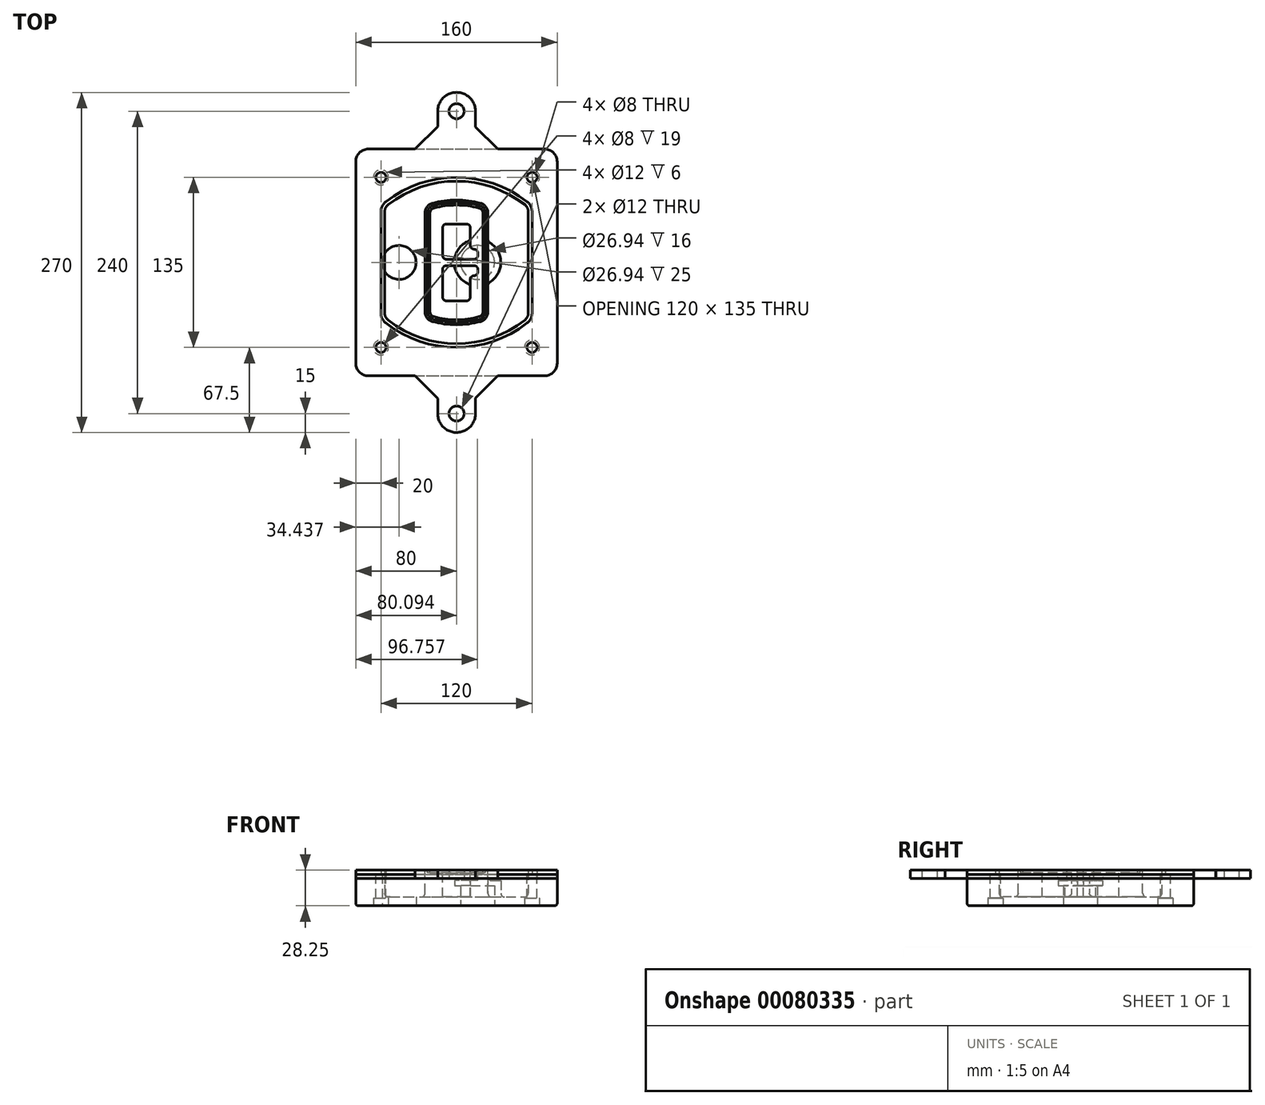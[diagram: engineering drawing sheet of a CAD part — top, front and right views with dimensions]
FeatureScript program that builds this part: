
annotation { "Feature Type Name" : "Feature", "Feature Type Description" : "" }
export const myFeature = defineFeature(function(context is Context, id is Id, definition is map)
    precondition{}
    {
        {
            var Q0;
            Q0=qCreatedBy(makeId("Top.planeOp"),FACE);
            var sketch = newSketch(context, id + "F0", { "sketchPlane" : qUnion([Q0])});
            skPoint(sketch, "E0.rect.middle", {"position": v(0, 0) * mm});
            skLineSegment(sketch, "E1.bottom", {"start": v(-70, -90) * mm, "end": v(70, -90) * mm});
            skLineSegment(sketch, "E1.top", {"start": v(-70, 90) * mm, "end": v(70, 90) * mm});
            skLineSegment(sketch, "E1.left", {"start": v(-80, -80) * mm, "end": v(-80, 80) * mm});
            skLineSegment(sketch, "E1.right", {"start": v(80, -80) * mm, "end": v(80, 80) * mm});
            skLineSegment(sketch, "E2", {"start": v(-80, 90) * mm, "end": v(80, -90) * mm, "construction": true});
            skLineSegment(sketch, "E3", {"start": v(80, 90) * mm, "end": v(-80, -90) * mm, "construction": true});
            skCircle(sketch, "E4", {"center": v(-60, 67.5) * mm, "radius": 4 * mm});
            skCircle(sketch, "E5", {"center": v(60, 67.5) * mm, "radius": 4 * mm});
            skCircle(sketch, "E6", {"center": v(60, -67.5) * mm, "radius": 4 * mm});
            skCircle(sketch, "E7", {"center": v(-60, -67.5) * mm, "radius": 4 * mm});
            skLineSegment(sketch, "E8", {"start": v(-60, 67.5) * mm, "end": v(60, 67.5) * mm, "construction": true});
            skLineSegment(sketch, "E9", {"start": v(60, 67.5) * mm, "end": v(60, -67.5) * mm, "construction": true});
            skLineSegment(sketch, "E10", {"start": v(60, -67.5) * mm, "end": v(-60, -67.5) * mm, "construction": true});
            skLineSegment(sketch, "E11", {"start": v(-60, -67.5) * mm, "end": v(-60, 67.5) * mm, "construction": true});
            skLineSegment(sketch, "E12", {"start": v(-60, 40.3) * mm, "end": v(-60, -40.3) * mm});
            skLineSegment(sketch, "E13", {"start": v(60, 40.3) * mm, "end": v(60, -40.3) * mm});
            skArc(sketch, "E14", {"start": v(56.15, 48.18) * mm, "mid": v(0, 67.5) * mm, "end": v(-56.15, 48.18) * mm});
            skArc(sketch, "E15", {"start": v(-56.15, -48.18) * mm, "mid": v(0, -67.5) * mm, "end": v(56.15, -48.18) * mm});
            skLineSegment(sketch, "E16", {"start": v(-60, 0) * mm, "end": v(60, 0) * mm, "construction": true});
            skPoint(sketch, "E17.visualSharp", {"position": v(-60, -45) * mm});
            skArc(sketch, "E17.filletArc", {"start": v(-60, -40.3) * mm, "mid": v(-58.99, -44.68) * mm, "end": v(-56.15, -48.18) * mm});
            skPoint(sketch, "E18.visualSharp", {"position": v(-60, 45) * mm});
            skArc(sketch, "E18.filletArc", {"start": v(-56.15, 48.18) * mm, "mid": v(-58.99, 44.68) * mm, "end": v(-60, 40.3) * mm});
            skPoint(sketch, "E19.visualSharp", {"position": v(60, 45) * mm});
            skArc(sketch, "E19.filletArc", {"start": v(60, 40.3) * mm, "mid": v(58.99, 44.68) * mm, "end": v(56.15, 48.18) * mm});
            skPoint(sketch, "E20.visualSharp", {"position": v(60, -45) * mm});
            skArc(sketch, "E20.filletArc", {"start": v(56.15, -48.18) * mm, "mid": v(58.99, -44.68) * mm, "end": v(60, -40.3) * mm});
            skPoint(sketch, "E21.visualSharp", {"position": v(-80, 90) * mm});
            skArc(sketch, "E21.filletArc", {"start": v(-70, 90) * mm, "mid": v(-77.07, 87.07) * mm, "end": v(-80, 80) * mm});
            skPoint(sketch, "E22.visualSharp", {"position": v(80, 90) * mm});
            skArc(sketch, "E22.filletArc", {"start": v(80, 80) * mm, "mid": v(77.07, 87.07) * mm, "end": v(70, 90) * mm});
            skPoint(sketch, "E23.visualSharp", {"position": v(80, -90) * mm});
            skArc(sketch, "E23.filletArc", {"start": v(70, -90) * mm, "mid": v(77.07, -87.07) * mm, "end": v(80, -80) * mm});
            skPoint(sketch, "E24.visualSharp", {"position": v(-80, -90) * mm});
            skArc(sketch, "E24.filletArc", {"start": v(-80, -80) * mm, "mid": v(-77.07, -87.07) * mm, "end": v(-70, -90) * mm});
            skArc(sketch, "E25.0", {"start": v(57, 40.3) * mm, "mid": v(56.3, 43.36) * mm, "end": v(54.3, 45.81) * mm});
            skLineSegment(sketch, "E25.1", {"start": v(57, 40.3) * mm, "end": v(57, -40.3) * mm});
            skArc(sketch, "E25.2", {"start": v(54.3, -45.81) * mm, "mid": v(56.3, -43.36) * mm, "end": v(57, -40.3) * mm});
            skArc(sketch, "E25.3", {"start": v(-54.3, -45.81) * mm, "mid": v(0, -64.5) * mm, "end": v(54.3, -45.81) * mm});
            skArc(sketch, "E25.4", {"start": v(-57, -40.3) * mm, "mid": v(-56.3, -43.36) * mm, "end": v(-54.3, -45.81) * mm});
            skArc(sketch, "E25.5", {"start": v(54.3, 45.81) * mm, "mid": v(0, 64.5) * mm, "end": v(-54.3, 45.81) * mm});
            skLineSegment(sketch, "E25.6", {"start": v(-57, 40.3) * mm, "end": v(-57, -40.3) * mm});
            skArc(sketch, "E25.7", {"start": v(-54.3, 45.81) * mm, "mid": v(-56.3, 43.36) * mm, "end": v(-57, 40.3) * mm});
            skArc(sketch, "E26.0", {"start": v(-58.62, 51.33) * mm, "mid": v(-62.58, 46.43) * mm, "end": v(-64, 40.3) * mm});
            skArc(sketch, "E26.1", {"start": v(58.62, 51.33) * mm, "mid": v(0, 71.5) * mm, "end": v(-58.62, 51.33) * mm});
            skArc(sketch, "E26.2", {"start": v(64, 40.3) * mm, "mid": v(62.58, 46.43) * mm, "end": v(58.62, 51.33) * mm});
            skLineSegment(sketch, "E26.3", {"start": v(64, 40.3) * mm, "end": v(64, -40.3) * mm});
            skArc(sketch, "E26.4", {"start": v(58.62, -51.33) * mm, "mid": v(62.58, -46.43) * mm, "end": v(64, -40.3) * mm});
            skLineSegment(sketch, "E26.5", {"start": v(-64, 40.3) * mm, "end": v(-64, -40.3) * mm});
            skArc(sketch, "E26.6", {"start": v(-58.62, -51.33) * mm, "mid": v(0, -71.5) * mm, "end": v(58.62, -51.33) * mm});
            skArc(sketch, "E26.7", {"start": v(-64, -40.3) * mm, "mid": v(-62.58, -46.43) * mm, "end": v(-58.62, -51.33) * mm});
            skSolve(sketch);
        }
        {
            var Q0;
            Q0=makeQuery(id+"F0.imprint","IMPRINT",FACE,{"disambiguationData":[TD([[makeQuery(id+"F0.imprint","IMPRINT",EDGE,{"derivedFrom":sQuery(id+"F0.wireOp",EDGE,"E1.bottom")}),1.0]])]});
            var Q1;
            Q1=makeQuery(id+"F0.imprint","IMPRINT",FACE,{"disambiguationData":[TD([[makeQuery(id+"F0.imprint","IMPRINT",EDGE,{"derivedFrom":sQuery(id+"F0.wireOp",EDGE,"E12")}),1.0]])]});
            var Q2;
            Q2=makeQuery(id+"F0.imprint","IMPRINT",FACE,{"disambiguationData":[TD([[makeQuery(id+"F0.imprint","IMPRINT",EDGE,{"derivedFrom":sQuery(id+"F0.wireOp",EDGE,"E25.0")}),1.0]])]});
            var Q3;
            Q3=makeQuery(id+"F0.imprint","IMPRINT",FACE,{"disambiguationData":[TD([[makeQuery(id+"F0.imprint","IMPRINT",EDGE,{"derivedFrom":sQuery(id+"F0.wireOp",EDGE,"E12")}),-1.0]])]});
            extrude(context, id + "F1", {"entities" : qUnion([Q0, Q1, Q2, Q3]), "oppositeDirection" : true, "depth" : 25 * mm});
        }
        {
            var Q0;
            Q0=makeQuery(id+"F0.imprint","IMPRINT",FACE,{"disambiguationData":[TD([[makeQuery(id+"F0.imprint","IMPRINT",EDGE,{"derivedFrom":sQuery(id+"F0.wireOp",EDGE,"E12")}),1.0]])]});
            extrude(context, id + "F2", {"entities" : qUnion([Q0]), "operationType" : NewBodyOperationType.ADD, "depth" : 3 * mm});
        }
        {
            var Q0;
            Q0=makeQuery(id+"F0.imprint","IMPRINT",FACE,{"disambiguationData":[TD([[makeQuery(id+"F0.imprint","IMPRINT",EDGE,{"derivedFrom":sQuery(id+"F0.wireOp",EDGE,"E25.0")}),1.0]])]});
            extrude(context, id + "F3", {"entities" : qUnion([Q0]), "operationType" : NewBodyOperationType.REMOVE, "oppositeDirection" : true, "depth" : 18 * mm});
        }
        {
            var Q0;
            Q0=makeQuery(id+"F2.opExtrude","CAP_FACE",FACE,{"disambiguationData":[OSD([sQuery(id+"F0.wireOp",EDGE,"E12"),sQuery(id+"F0.wireOp",EDGE,"E13"),sQuery(id+"F0.wireOp",EDGE,"E14"),sQuery(id+"F0.wireOp",EDGE,"E15"),sQuery(id+"F0.wireOp",EDGE,"E17.filletArc"),sQuery(id+"F0.wireOp",EDGE,"E18.filletArc"),sQuery(id+"F0.wireOp",EDGE,"E19.filletArc"),sQuery(id+"F0.wireOp",EDGE,"E20.filletArc"),sQuery(id+"F0.wireOp",EDGE,"E25.0"),sQuery(id+"F0.wireOp",EDGE,"E25.1"),sQuery(id+"F0.wireOp",EDGE,"E25.2"),sQuery(id+"F0.wireOp",EDGE,"E25.3"),sQuery(id+"F0.wireOp",EDGE,"E25.4"),sQuery(id+"F0.wireOp",EDGE,"E25.5"),sQuery(id+"F0.wireOp",EDGE,"E25.6"),sQuery(id+"F0.wireOp",EDGE,"E25.7")])],"isStart":false});
            var sketch = newSketch(context, id + "F4", { "sketchPlane" : qUnion([Q0])});
            skArc(sketch, "E27.0", {"start": v(-19.08, -46.97) * mm, "mid": v(0, -49.5) * mm, "end": v(19.08, -46.97) * mm});
            skArc(sketch, "E28.0", {"start": v(19.08, 46.97) * mm, "mid": v(0, 49.5) * mm, "end": v(-19.08, 46.97) * mm});
            skLineSegment(sketch, "E29", {"start": v(-25, 39.25) * mm, "end": v(-25, -39.25) * mm});
            skLineSegment(sketch, "E30", {"start": v(25, 39.25) * mm, "end": v(25, -39.25) * mm});
            skLineSegment(sketch, "E31", {"start": v(-25, 45.1) * mm, "end": v(25, 45.1) * mm, "construction": true});
            skLineSegment(sketch, "E32", {"start": v(-25, -45.1) * mm, "end": v(25, -45.1) * mm, "construction": true});
            skPoint(sketch, "E33.visualSharp", {"position": v(-25, 45.1) * mm});
            skArc(sketch, "E33.filletArc", {"start": v(-19.08, 46.97) * mm, "mid": v(-23.35, 44.11) * mm, "end": v(-25, 39.25) * mm});
            skPoint(sketch, "E34.visualSharp", {"position": v(25, 45.1) * mm});
            skArc(sketch, "E34.filletArc", {"start": v(25, 39.25) * mm, "mid": v(23.35, 44.11) * mm, "end": v(19.08, 46.97) * mm});
            skPoint(sketch, "E35.visualSharp", {"position": v(25, -45.1) * mm});
            skArc(sketch, "E35.filletArc", {"start": v(19.08, -46.97) * mm, "mid": v(23.35, -44.11) * mm, "end": v(25, -39.25) * mm});
            skPoint(sketch, "E36.visualSharp", {"position": v(-25, -45.1) * mm});
            skArc(sketch, "E36.filletArc", {"start": v(-25, -39.25) * mm, "mid": v(-23.35, -44.11) * mm, "end": v(-19.08, -46.97) * mm});
            skArc(sketch, "E37.0", {"start": v(54.3, 45.81) * mm, "mid": v(0, 64.5) * mm, "end": v(-54.3, 45.81) * mm});
            skArc(sketch, "E37.1", {"start": v(-54.3, 45.81) * mm, "mid": v(-56.3, 43.36) * mm, "end": v(-57, 40.3) * mm});
            skLineSegment(sketch, "E37.2", {"start": v(-57, 40.3) * mm, "end": v(-57, -40.3) * mm});
            skArc(sketch, "E37.3", {"start": v(-57, -40.3) * mm, "mid": v(-56.3, -43.36) * mm, "end": v(-54.3, -45.81) * mm});
            skArc(sketch, "E37.4", {"start": v(-54.3, -45.81) * mm, "mid": v(0, -64.5) * mm, "end": v(54.3, -45.81) * mm});
            skArc(sketch, "E37.5", {"start": v(54.3, -45.81) * mm, "mid": v(56.3, -43.36) * mm, "end": v(57, -40.3) * mm});
            skLineSegment(sketch, "E37.6", {"start": v(57, 40.3) * mm, "end": v(57, -40.3) * mm});
            skArc(sketch, "E37.7", {"start": v(57, 40.3) * mm, "mid": v(56.3, 43.36) * mm, "end": v(54.3, 45.81) * mm});
            skLineSegment(sketch, "E38.0", {"start": v(23, 39.25) * mm, "end": v(23, -39.25) * mm});
            skArc(sketch, "E38.1", {"start": v(18.56, -45.04) * mm, "mid": v(21.76, -42.9) * mm, "end": v(23, -39.25) * mm});
            skArc(sketch, "E38.2", {"start": v(-18.56, -45.04) * mm, "mid": v(0, -47.5) * mm, "end": v(18.56, -45.04) * mm});
            skArc(sketch, "E38.3", {"start": v(-23, -39.25) * mm, "mid": v(-21.76, -42.9) * mm, "end": v(-18.56, -45.04) * mm});
            skLineSegment(sketch, "E38.4", {"start": v(-23, 39.25) * mm, "end": v(-23, -39.25) * mm});
            skArc(sketch, "E38.5", {"start": v(23, 39.25) * mm, "mid": v(21.76, 42.9) * mm, "end": v(18.56, 45.04) * mm});
            skArc(sketch, "E38.6", {"start": v(-18.56, 45.04) * mm, "mid": v(-21.76, 42.9) * mm, "end": v(-23, 39.25) * mm});
            skArc(sketch, "E38.7", {"start": v(18.56, 45.04) * mm, "mid": v(0, 47.5) * mm, "end": v(-18.56, 45.04) * mm});
            skArc(sketch, "E39.0", {"start": v(21, 39.25) * mm, "mid": v(20.18, 41.68) * mm, "end": v(18.04, 43.1) * mm});
            skLineSegment(sketch, "E39.1", {"start": v(21, 39.25) * mm, "end": v(21, -39.25) * mm});
            skArc(sketch, "E39.2", {"start": v(18.04, -43.1) * mm, "mid": v(20.18, -41.68) * mm, "end": v(21, -39.25) * mm});
            skArc(sketch, "E39.3", {"start": v(-18.04, -43.1) * mm, "mid": v(0, -45.5) * mm, "end": v(18.04, -43.1) * mm});
            skArc(sketch, "E39.4", {"start": v(-21, -39.25) * mm, "mid": v(-20.18, -41.68) * mm, "end": v(-18.04, -43.1) * mm});
            skArc(sketch, "E39.5", {"start": v(18.04, 43.1) * mm, "mid": v(0, 45.5) * mm, "end": v(-18.04, 43.1) * mm});
            skLineSegment(sketch, "E39.6", {"start": v(-21, 39.25) * mm, "end": v(-21, -39.25) * mm});
            skArc(sketch, "E39.7", {"start": v(-18.04, 43.1) * mm, "mid": v(-20.18, 41.68) * mm, "end": v(-21, 39.25) * mm});
            skLineSegment(sketch, "E40", {"start": v(-25, 0) * mm, "end": v(25, 0) * mm, "construction": true});
            skLineSegment(sketch, "E41", {"start": v(-11, 5.5) * mm, "end": v(-11, 27.5) * mm});
            skLineSegment(sketch, "E42", {"start": v(-8, 30.5) * mm, "end": v(8, 30.5) * mm});
            skLineSegment(sketch, "E43", {"start": v(11, 27.5) * mm, "end": v(11, 13.5) * mm});
            skLineSegment(sketch, "E44", {"start": v(14, 10.5) * mm, "end": v(14, 10.5) * mm});
            skLineSegment(sketch, "E45", {"start": v(17, 7.5) * mm, "end": v(17, 5.5) * mm});
            skLineSegment(sketch, "E46", {"start": v(14, 2.5) * mm, "end": v(-8, 2.5) * mm});
            skPoint(sketch, "E47.visualSharp", {"position": v(-11, 30.5) * mm});
            skArc(sketch, "E47.filletArc", {"start": v(-8, 30.5) * mm, "mid": v(-10.12, 29.62) * mm, "end": v(-11, 27.5) * mm});
            skPoint(sketch, "E48.visualSharp", {"position": v(11, 30.5) * mm});
            skArc(sketch, "E48.filletArc", {"start": v(11, 27.5) * mm, "mid": v(10.12, 29.62) * mm, "end": v(8, 30.5) * mm});
            skPoint(sketch, "E49.visualSharp", {"position": v(11, 10.5) * mm});
            skArc(sketch, "E49.filletArc", {"start": v(11, 13.5) * mm, "mid": v(11.88, 11.38) * mm, "end": v(14, 10.5) * mm});
            skPoint(sketch, "E50.visualSharp", {"position": v(17, 10.5) * mm});
            skArc(sketch, "E50.filletArc", {"start": v(17, 7.5) * mm, "mid": v(16.12, 9.62) * mm, "end": v(14, 10.5) * mm});
            skPoint(sketch, "E51.visualSharp", {"position": v(17, 2.5) * mm});
            skArc(sketch, "E51.filletArc", {"start": v(14, 2.5) * mm, "mid": v(16.12, 3.38) * mm, "end": v(17, 5.5) * mm});
            skPoint(sketch, "E52.visualSharp", {"position": v(-11, 2.5) * mm});
            skArc(sketch, "E52.filletArc", {"start": v(-11, 5.5) * mm, "mid": v(-10.12, 3.38) * mm, "end": v(-8, 2.5) * mm});
            skLineSegment(sketch, "E53.0.MirrorCS", {"start": v(14, -2.5) * mm, "end": v(-8, -2.5) * mm});
            skArc(sketch, "E54.0.MirrorCS", {"start": v(-11, -5.5) * mm, "mid": v(-10.12, -3.38) * mm, "end": v(-8, -2.5) * mm});
            skLineSegment(sketch, "E55.0.MirrorCS", {"start": v(-11, -5.5) * mm, "end": v(-11, -27.5) * mm});
            skArc(sketch, "E56.0.MirrorCS", {"start": v(-8, -30.5) * mm, "mid": v(-10.12, -29.62) * mm, "end": v(-11, -27.5) * mm});
            skLineSegment(sketch, "E57.0.MirrorCS", {"start": v(-8, -30.5) * mm, "end": v(8, -30.5) * mm});
            skArc(sketch, "E58.0.MirrorCS", {"start": v(11, -27.5) * mm, "mid": v(10.12, -29.62) * mm, "end": v(8, -30.5) * mm});
            skLineSegment(sketch, "E59.0.MirrorCS", {"start": v(11, -27.5) * mm, "end": v(11, -13.5) * mm});
            skArc(sketch, "E60.0.MirrorCS", {"start": v(11, -13.5) * mm, "mid": v(11.88, -11.38) * mm, "end": v(14, -10.5) * mm});
            skArc(sketch, "E61.0.MirrorCS", {"start": v(17, -7.5) * mm, "mid": v(16.12, -9.62) * mm, "end": v(14, -10.5) * mm});
            skLineSegment(sketch, "E62.0.MirrorCS", {"start": v(17, -7.5) * mm, "end": v(17, -5.5) * mm});
            skArc(sketch, "E63.0.MirrorCS", {"start": v(14, -2.5) * mm, "mid": v(16.12, -3.38) * mm, "end": v(17, -5.5) * mm});
            skSolve(sketch);
        }
        {
            var Q0;
            Q0=makeQuery(id+"F4.imprint","IMPRINT",FACE,{"disambiguationData":[TD([[makeQuery(id+"F4.imprint","IMPRINT",EDGE,{"derivedFrom":sQuery(id+"F4.wireOp",EDGE,"E27.0")}),1.0]])]});
            var Q1;
            Q1=makeQuery(id+"F4.imprint","IMPRINT",FACE,{"disambiguationData":[TD([[makeQuery(id+"F4.imprint","IMPRINT",EDGE,{"derivedFrom":sQuery(id+"F4.wireOp",EDGE,"E38.0")}),-1.0]])]});
            var Q2;
            Q2=makeQuery(id+"F4.imprint","IMPRINT",FACE,{"disambiguationData":[TD([[makeQuery(id+"F4.imprint","IMPRINT",EDGE,{"derivedFrom":sQuery(id+"F4.wireOp",EDGE,"E39.0")}),1.0]])]});
            extrude(context, id + "F5", {"entities" : qUnion([Q0, Q1, Q2]), "operationType" : NewBodyOperationType.ADD, "endBound" : BoundingType.UP_TO_NEXT, "oppositeDirection" : true, "depth" : 25 * mm});
        }
        {
            var Q0;
            Q0=makeQuery(id+"F4.imprint","IMPRINT",FACE,{"disambiguationData":[TD([[makeQuery(id+"F4.imprint","IMPRINT",EDGE,{"derivedFrom":sQuery(id+"F4.wireOp",EDGE,"E38.0")}),-1.0]])]});
            extrude(context, id + "F6", {"entities" : qUnion([Q0]), "operationType" : NewBodyOperationType.REMOVE, "oppositeDirection" : true, "depth" : 2 * mm});
        }
        {
            var Q0;
            Q0=makeQuery(id+"F1.opExtrude","CAP_FACE",FACE,{"disambiguationData":[OSD([sQuery(id+"F0.wireOp",EDGE,"E1.bottom"),sQuery(id+"F0.wireOp",EDGE,"E1.top"),sQuery(id+"F0.wireOp",EDGE,"E1.left"),sQuery(id+"F0.wireOp",EDGE,"E1.right"),sQuery(id+"F0.wireOp",EDGE,"E4"),sQuery(id+"F0.wireOp",EDGE,"E5"),sQuery(id+"F0.wireOp",EDGE,"E6"),sQuery(id+"F0.wireOp",EDGE,"E7"),sQuery(id+"F0.wireOp",EDGE,"E21.filletArc"),sQuery(id+"F0.wireOp",EDGE,"E22.filletArc"),sQuery(id+"F0.wireOp",EDGE,"E23.filletArc"),sQuery(id+"F0.wireOp",EDGE,"E24.filletArc")])],"isStart":false});
            var sketch = newSketch(context, id + "F7", { "sketchPlane" : qUnion([Q0])});
            skCircle(sketch, "E64", {"center": v(16.76, 0) * mm, "radius": 13.47 * mm});
            skCircle(sketch, "E65", {"center": v(-45.56, 0) * mm, "radius": 13.47 * mm});
            skLineSegment(sketch, "E66", {"start": v(80, 0) * mm, "end": v(-80, 0) * mm});
            skCircle(sketch, "E67", {"center": v(16.76, 0) * mm, "radius": 18.47 * mm});
            skCircle(sketch, "E68", {"center": v(60, -67.5) * mm, "radius": 6 * mm});
            skCircle(sketch, "E69", {"center": v(-60, -67.5) * mm, "radius": 6 * mm});
            skCircle(sketch, "E70", {"center": v(-60, 67.5) * mm, "radius": 6 * mm});
            skCircle(sketch, "E71", {"center": v(60, 67.5) * mm, "radius": 6 * mm});
            skSolve(sketch);
        }
        {
            var Q0;
            {var subQ1=sQuery(id+"F7.wireOp",EDGE,"E66");var subQ4=sQuery(id+"F7.wireOp",EDGE,"E64");var subQ6=makeQuery(id+"F7.imprint","INTERSECT",VERTEX,{"disambiguationData":[OD(0.0)],"derivedFrom":[subQ4,subQ1]});Q0=makeQuery(id+"F7.imprint","IMPRINT",FACE,{"disambiguationData":[TD([[makeQuery(id+"F7.imprint","IMPRINT",EDGE,{"disambiguationData":[TD([[subQ6,-1.0]])],"derivedFrom":subQ4}),-1.0]])]});}
            var Q1;
            {var subQ0=sQuery(id+"F7.wireOp",EDGE,"E66");var subQ1=sQuery(id+"F7.wireOp",EDGE,"E64");var subQ3=makeQuery(id+"F7.imprint","INTERSECT",VERTEX,{"disambiguationData":[OD(0.0)],"derivedFrom":[subQ1,subQ0]});Q1=makeQuery(id+"F7.imprint","IMPRINT",FACE,{"disambiguationData":[TD([[makeQuery(id+"F7.imprint","IMPRINT",EDGE,{"disambiguationData":[TD([[subQ3,-1.0]])],"derivedFrom":subQ1}),1.0]])]});}
            var Q2;
            {var subQ0=sQuery(id+"F7.wireOp",EDGE,"E66");var subQ1=sQuery(id+"F7.wireOp",EDGE,"E64");var subQ3=makeQuery(id+"F7.imprint","INTERSECT",VERTEX,{"disambiguationData":[OD(0.0)],"derivedFrom":[subQ1,subQ0]});Q2=makeQuery(id+"F7.imprint","IMPRINT",FACE,{"disambiguationData":[TD([[makeQuery(id+"F7.imprint","IMPRINT",EDGE,{"disambiguationData":[TD([[subQ3,1.0]])],"derivedFrom":subQ1}),1.0]])]});}
            var Q3;
            {var subQ1=sQuery(id+"F7.wireOp",EDGE,"E66");var subQ4=sQuery(id+"F7.wireOp",EDGE,"E64");var subQ6=makeQuery(id+"F7.imprint","INTERSECT",VERTEX,{"disambiguationData":[OD(0.0)],"derivedFrom":[subQ4,subQ1]});Q3=makeQuery(id+"F7.imprint","IMPRINT",FACE,{"disambiguationData":[TD([[makeQuery(id+"F7.imprint","IMPRINT",EDGE,{"disambiguationData":[TD([[subQ6,1.0]])],"derivedFrom":subQ4}),-1.0]])]});}
            extrude(context, id + "F8", {"entities" : qUnion([Q0, Q1, Q2, Q3]), "operationType" : NewBodyOperationType.ADD, "oppositeDirection" : true, "depth" : 20 * mm});
        }
        {
            var Q0;
            {var subQ0=sQuery(id+"F7.wireOp",EDGE,"E66");var subQ1=sQuery(id+"F7.wireOp",EDGE,"E64");var subQ3=makeQuery(id+"F7.imprint","INTERSECT",VERTEX,{"disambiguationData":[OD(0.0)],"derivedFrom":[subQ1,subQ0]});Q0=makeQuery(id+"F7.imprint","IMPRINT",FACE,{"disambiguationData":[TD([[makeQuery(id+"F7.imprint","IMPRINT",EDGE,{"disambiguationData":[TD([[subQ3,-1.0]])],"derivedFrom":subQ1}),1.0]])]});}
            var Q1;
            {var subQ0=sQuery(id+"F7.wireOp",EDGE,"E66");var subQ1=sQuery(id+"F7.wireOp",EDGE,"E64");var subQ3=makeQuery(id+"F7.imprint","INTERSECT",VERTEX,{"disambiguationData":[OD(0.0)],"derivedFrom":[subQ1,subQ0]});Q1=makeQuery(id+"F7.imprint","IMPRINT",FACE,{"disambiguationData":[TD([[makeQuery(id+"F7.imprint","IMPRINT",EDGE,{"disambiguationData":[TD([[subQ3,1.0]])],"derivedFrom":subQ1}),1.0]])]});}
            extrude(context, id + "F9", {"entities" : qUnion([Q0, Q1]), "operationType" : NewBodyOperationType.REMOVE, "oppositeDirection" : true, "depth" : 16 * mm});
        }
        {
            var Q0;
            {var subQ0=sQuery(id+"F7.wireOp",EDGE,"E66");var subQ1=sQuery(id+"F7.wireOp",EDGE,"E65");var subQ3=makeQuery(id+"F7.imprint","INTERSECT",VERTEX,{"disambiguationData":[OD(0.0)],"derivedFrom":[subQ1,subQ0]});Q0=makeQuery(id+"F7.imprint","IMPRINT",FACE,{"disambiguationData":[TD([[makeQuery(id+"F7.imprint","IMPRINT",EDGE,{"disambiguationData":[TD([[subQ3,-1.0]])],"derivedFrom":subQ1}),1.0]])]});}
            var Q1;
            {var subQ0=sQuery(id+"F7.wireOp",EDGE,"E66");var subQ1=sQuery(id+"F7.wireOp",EDGE,"E65");var subQ3=makeQuery(id+"F7.imprint","INTERSECT",VERTEX,{"disambiguationData":[OD(0.0)],"derivedFrom":[subQ1,subQ0]});Q1=makeQuery(id+"F7.imprint","IMPRINT",FACE,{"disambiguationData":[TD([[makeQuery(id+"F7.imprint","IMPRINT",EDGE,{"disambiguationData":[TD([[subQ3,1.0]])],"derivedFrom":subQ1}),1.0]])]});}
            extrude(context, id + "F10", {"entities" : qUnion([Q0, Q1]), "operationType" : NewBodyOperationType.REMOVE, "oppositeDirection" : true, "depth" : 25 * mm});
        }
        {
            var Q0;
            Q0=makeQuery(id+"F7.imprint","IMPRINT",FACE,{"disambiguationData":[TD([[makeQuery(id+"F7.imprint","IMPRINT",EDGE,{"derivedFrom":sQuery(id+"F7.wireOp",EDGE,"E68")}),1.0]])]});
            var Q1;
            Q1=makeQuery(id+"F7.imprint","IMPRINT",FACE,{"disambiguationData":[TD([[makeQuery(id+"F7.imprint","IMPRINT",EDGE,{"derivedFrom":makeQuery(id+"F1.opExtrude","CAP_EDGE",EDGE,{"disambiguationData":[OSD([sQuery(id+"F0.wireOp",EDGE,"E5")])],"isStart":false})}),-1.0]])]});
            var Q2;
            Q2=makeQuery(id+"F7.imprint","IMPRINT",FACE,{"disambiguationData":[TD([[makeQuery(id+"F7.imprint","IMPRINT",EDGE,{"derivedFrom":sQuery(id+"F7.wireOp",EDGE,"E69")}),1.0]])]});
            var Q3;
            Q3=makeQuery(id+"F7.imprint","IMPRINT",FACE,{"disambiguationData":[TD([[makeQuery(id+"F7.imprint","IMPRINT",EDGE,{"derivedFrom":makeQuery(id+"F1.opExtrude","CAP_EDGE",EDGE,{"disambiguationData":[OSD([sQuery(id+"F0.wireOp",EDGE,"E4")])],"isStart":false})}),-1.0]])]});
            var Q4;
            Q4=makeQuery(id+"F7.imprint","IMPRINT",FACE,{"disambiguationData":[TD([[makeQuery(id+"F7.imprint","IMPRINT",EDGE,{"derivedFrom":sQuery(id+"F7.wireOp",EDGE,"E70")}),1.0]])]});
            var Q5;
            Q5=makeQuery(id+"F7.imprint","IMPRINT",FACE,{"disambiguationData":[TD([[makeQuery(id+"F7.imprint","IMPRINT",EDGE,{"derivedFrom":makeQuery(id+"F1.opExtrude","CAP_EDGE",EDGE,{"disambiguationData":[OSD([sQuery(id+"F0.wireOp",EDGE,"E7")])],"isStart":false})}),-1.0]])]});
            var Q6;
            Q6=makeQuery(id+"F7.imprint","IMPRINT",FACE,{"disambiguationData":[TD([[makeQuery(id+"F7.imprint","IMPRINT",EDGE,{"derivedFrom":sQuery(id+"F7.wireOp",EDGE,"E71")}),1.0]])]});
            var Q7;
            Q7=makeQuery(id+"F7.imprint","IMPRINT",FACE,{"disambiguationData":[TD([[makeQuery(id+"F7.imprint","IMPRINT",EDGE,{"derivedFrom":makeQuery(id+"F1.opExtrude","CAP_EDGE",EDGE,{"disambiguationData":[OSD([sQuery(id+"F0.wireOp",EDGE,"E6")])],"isStart":false})}),-1.0]])]});
            extrude(context, id + "F11", {"entities" : qUnion([Q0, Q1, Q2, Q3, Q4, Q5, Q6, Q7]), "operationType" : NewBodyOperationType.REMOVE, "oppositeDirection" : true, "depth" : 6 * mm});
        }
        {
            var Q0;
            Q0=makeQuery(id+"F9.boolean.opBoolean","COPY",FACE,{"derivedFrom":makeQuery(id+"F9.opExtrude","CAP_FACE",FACE,{"disambiguationData":[OSD([sQuery(id+"F7.wireOp",EDGE,"E64")])],"isStart":false})});
            var sketch = newSketch(context, id + "F12", { "sketchPlane" : qUnion([Q0])});
            skArc(sketch, "E72.0", {"start": v(11, 17.55) * mm, "mid": v(2.57, 11.82) * mm, "end": v(-1.54, 2.5) * mm});
            skArc(sketch, "E72.1", {"start": v(-1.54, -2.5) * mm, "mid": v(2.57, -11.82) * mm, "end": v(11, -17.55) * mm});
            skLineSegment(sketch, "E73", {"start": v(-1.54, -2.5) * mm, "end": v(14, -2.5) * mm});
            skLineSegment(sketch, "E74.0", {"start": v(14, 2.5) * mm, "end": v(-1.54, 2.5) * mm});
            skArc(sketch, "E74.1", {"start": v(14, 2.5) * mm, "mid": v(16.12, 3.38) * mm, "end": v(17, 5.5) * mm});
            skLineSegment(sketch, "E74.2", {"start": v(17, 7.5) * mm, "end": v(17, 5.5) * mm});
            skArc(sketch, "E74.3", {"start": v(17, 7.5) * mm, "mid": v(16.12, 9.62) * mm, "end": v(14, 10.5) * mm});
            skArc(sketch, "E74.4", {"start": v(11, 13.5) * mm, "mid": v(11.88, 11.38) * mm, "end": v(14, 10.5) * mm});
            skLineSegment(sketch, "E74.5", {"start": v(11, 17.55) * mm, "end": v(11, 13.5) * mm});
            skLineSegment(sketch, "E74.7", {"start": v(14, -2.5) * mm, "end": v(-1.54, -2.5) * mm});
            skArc(sketch, "E74.8", {"start": v(14, -2.5) * mm, "mid": v(16.12, -3.38) * mm, "end": v(17, -5.5) * mm});
            skLineSegment(sketch, "E74.9", {"start": v(17, -7.5) * mm, "end": v(17, -5.5) * mm});
            skArc(sketch, "E74.10", {"start": v(17, -7.5) * mm, "mid": v(16.12, -9.62) * mm, "end": v(14, -10.5) * mm});
            skArc(sketch, "E74.11", {"start": v(11, -13.5) * mm, "mid": v(11.88, -11.38) * mm, "end": v(14, -10.5) * mm});
            skLineSegment(sketch, "E74.12", {"start": v(11, -17.55) * mm, "end": v(11, -13.5) * mm});
            skPoint(sketch, "E75.orphan", {"position": v(11, -27.5) * mm});
            skPoint(sketch, "E76.orphan", {"position": v(-8, -2.5) * mm});
            skPoint(sketch, "E77.orphan", {"position": v(-8, 2.5) * mm});
            skPoint(sketch, "E78.orphan", {"position": v(11, 27.5) * mm});
            skSolve(sketch);
        }
        {
            var Q0;
            {var subQ7=sQuery(id+"F12.wireOp",EDGE,"E72.0");var subQ14=sQuery(id+"F12.wireOp",EDGE,"E72.1");var subQ16=sQuery(id+"F12.wireOp",EDGE,"E74.1");var subQ18=sQuery(id+"F12.wireOp",EDGE,"E74.8");Q0=qUnion([makeQuery(id+"F12.imprint","IMPRINT",FACE,{"disambiguationData":[TD([[makeQuery(id+"F12.imprint","IMPRINT",EDGE,{"derivedFrom":subQ7}),1.0]])]}),makeQuery(id+"F12.imprint","IMPRINT",FACE,{"disambiguationData":[TD([[makeQuery(id+"F12.imprint","IMPRINT",EDGE,{"derivedFrom":subQ14}),1.0]])]}),makeQuery(id+"F12.imprint","IMPRINT",FACE,{"disambiguationData":[TD([[makeQuery(id+"F12.imprint","IMPRINT",EDGE,{"derivedFrom":subQ16}),1.0]])]}),makeQuery(id+"F12.imprint","IMPRINT",FACE,{"disambiguationData":[TD([[makeQuery(id+"F12.imprint","IMPRINT",EDGE,{"derivedFrom":subQ18}),-1.0]])]})]);}
            var Q1;
            Q1=makeQuery(id+"F5.boolean.opBoolean","SPLIT",FACE,{"disambiguationData":[TD([makeQuery(id+"F5.opExtrude","SWEPT_FACE",FACE,{"disambiguationData":[OSD([sQuery(id+"F4.wireOp",EDGE,"E41")])]})])],"derivedFrom":makeQuery(id+"F3.boolean.opBoolean","COPY",FACE,{"derivedFrom":makeQuery(id+"F3.opExtrude","CAP_FACE",FACE,{"disambiguationData":[OSD([sQuery(id+"F0.wireOp",EDGE,"E25.0"),sQuery(id+"F0.wireOp",EDGE,"E25.1"),sQuery(id+"F0.wireOp",EDGE,"E25.2"),sQuery(id+"F0.wireOp",EDGE,"E25.3"),sQuery(id+"F0.wireOp",EDGE,"E25.4"),sQuery(id+"F0.wireOp",EDGE,"E25.5"),sQuery(id+"F0.wireOp",EDGE,"E25.6"),sQuery(id+"F0.wireOp",EDGE,"E25.7")])],"isStart":false})})});
            extrude(context, id + "F13", {"entities" : qUnion([Q0]), "operationType" : NewBodyOperationType.REMOVE, "endBound" : BoundingType.UP_TO_SURFACE, "endBoundEntityFace" : qUnion([Q1]), "depth" : 25 * mm});
        }
        {
            var Q0;
            Q0=makeQuery(id+"F3.boolean.opBoolean","COPY",EDGE,{"derivedFrom":makeQuery(id+"F3.opExtrude","CAP_EDGE",EDGE,{"disambiguationData":[OSD([sQuery(id+"F0.wireOp",EDGE,"E25.6")])],"isStart":false})});
            var Q1;
            Q1=makeQuery(id+"F8.boolean.opBoolean","INTERSECT",EDGE,{"derivedFrom":[makeQuery(id+"F5.opExtrude","SWEPT_FACE",FACE,{"disambiguationData":[OSD([sQuery(id+"F4.wireOp",EDGE,"E30")])]}),makeQuery(id+"F8.opExtrude","CAP_FACE",FACE,{"disambiguationData":[OSD([sQuery(id+"F7.wireOp",EDGE,"E67")])],"isStart":false})]});
            var Q2;
            Q2=makeQuery(id+"F8.boolean.opBoolean","INTERSECT",EDGE,{"disambiguationData":[OD(1.0)],"derivedFrom":[makeQuery(id+"F5.opExtrude","SWEPT_FACE",FACE,{"disambiguationData":[OSD([sQuery(id+"F4.wireOp",EDGE,"E30")])]}),makeQuery(id+"F8.opExtrude","SWEPT_FACE",FACE,{"disambiguationData":[OSD([sQuery(id+"F7.wireOp",EDGE,"E67")])]})]});
            var Q3;
            {var subQ0=sQuery(id+"F4.wireOp",EDGE,"E30");Q3=makeQuery(id+"F8.boolean.opBoolean","SPLIT",EDGE,{"disambiguationData":[TD([makeQuery(id+"F5.opExtrude","SWEPT_FACE",FACE,{"disambiguationData":[OSD([sQuery(id+"F4.wireOp",EDGE,"E35.filletArc")])]})])],"derivedFrom":makeQuery(id+"F5.opExtrude","CAP_EDGE",EDGE,{"disambiguationData":[OSD([subQ0])],"isStart":false})});}
            var Q4;
            {var subQ0=sQuery(id+"F0.wireOp",EDGE,"E25.7");var subQ1=sQuery(id+"F0.wireOp",EDGE,"E25.1");var subQ2=sQuery(id+"F0.wireOp",EDGE,"E25.6");var subQ3=sQuery(id+"F0.wireOp",EDGE,"E25.5");var subQ4=sQuery(id+"F0.wireOp",EDGE,"E25.4");var subQ5=sQuery(id+"F0.wireOp",EDGE,"E25.0");var subQ6=sQuery(id+"F0.wireOp",EDGE,"E25.2");var subQ7=sQuery(id+"F0.wireOp",EDGE,"E25.3");Q4=makeQuery(id+"F8.boolean.opBoolean","INTERSECT",EDGE,{"derivedFrom":[makeQuery(id+"F5.boolean.opBoolean","SPLIT",FACE,{"disambiguationData":[TD([makeQuery(id+"F2.opExtrude","SWEPT_FACE",FACE,{"disambiguationData":[OSD([subQ5])]})])],"derivedFrom":makeQuery(id+"F3.boolean.opBoolean","COPY",FACE,{"derivedFrom":makeQuery(id+"F3.opExtrude","CAP_FACE",FACE,{"disambiguationData":[OSD([subQ5,subQ1,subQ6,subQ7,subQ4,subQ3,subQ2,subQ0])],"isStart":false})})}),makeQuery(id+"F8.opExtrude","SWEPT_FACE",FACE,{"disambiguationData":[OSD([sQuery(id+"F7.wireOp",EDGE,"E67")])]})]});}
            var Q5;
            Q5=makeQuery(id+"F8.boolean.opBoolean","INTERSECT",EDGE,{"disambiguationData":[OD(0.0)],"derivedFrom":[makeQuery(id+"F5.opExtrude","SWEPT_FACE",FACE,{"disambiguationData":[OSD([sQuery(id+"F4.wireOp",EDGE,"E30")])]}),makeQuery(id+"F8.opExtrude","SWEPT_FACE",FACE,{"disambiguationData":[OSD([sQuery(id+"F7.wireOp",EDGE,"E67")])]})]});
            fillet(context, id + "F14", {"entities" : qUnion([Q0, Q1, Q2, Q3, Q4, Q5]), "radius" : 3 * mm, "tangentPropagation" : true, "allowEdgeOverflow" : false});
        }
        {
            var Q0;
            Q0=makeQuery(id+"F1.opExtrude","CAP_EDGE",EDGE,{"disambiguationData":[OSD([sQuery(id+"F0.wireOp",EDGE,"E1.bottom")])],"isStart":false});
            fillet(context, id + "F15", {"entities" : qUnion([Q0]), "radius" : 2 * mm, "tangentPropagation" : true, "allowEdgeOverflow" : false});
        }
        {
            var Q0;
            {var subQ0=sQuery(id+"F0.wireOp",EDGE,"E22.filletArc");var subQ1=sQuery(id+"F0.wireOp",EDGE,"E7");var subQ2=sQuery(id+"F0.wireOp",EDGE,"E6");var subQ3=sQuery(id+"F0.wireOp",EDGE,"E5");var subQ4=sQuery(id+"F0.wireOp",EDGE,"E4");var subQ5=sQuery(id+"F0.wireOp",EDGE,"E1.bottom");var subQ6=sQuery(id+"F0.wireOp",EDGE,"E21.filletArc");var subQ7=sQuery(id+"F0.wireOp",EDGE,"E1.top");var subQ8=sQuery(id+"F0.wireOp",EDGE,"E1.left");var subQ9=sQuery(id+"F0.wireOp",EDGE,"E1.right");var subQ10=sQuery(id+"F0.wireOp",EDGE,"E23.filletArc");var subQ11=sQuery(id+"F0.wireOp",EDGE,"E24.filletArc");Q0=makeQuery(id+"F2.boolean.opBoolean","SPLIT",FACE,{"disambiguationData":[TD([makeQuery(id+"F1.opExtrude","SWEPT_FACE",FACE,{"disambiguationData":[OSD([subQ5])]})])],"derivedFrom":makeQuery(id+"F1.opExtrude","CAP_FACE",FACE,{"disambiguationData":[OSD([subQ5,subQ7,subQ8,subQ9,subQ4,subQ3,subQ2,subQ1,subQ6,subQ0,subQ10,subQ11])],"isStart":true})});}
            var sketch = newSketch(context, id + "F16", { "sketchPlane" : qUnion([Q0])});
            skArc(sketch, "E79.0", {"start": v(56.15, 48.18) * mm, "mid": v(0, 67.5) * mm, "end": v(-56.15, 48.18) * mm});
            skArc(sketch, "E79.1", {"start": v(-56.15, 48.18) * mm, "mid": v(-58.99, 44.68) * mm, "end": v(-60, 40.3) * mm});
            skLineSegment(sketch, "E79.2", {"start": v(-60, 40.3) * mm, "end": v(-60, -40.3) * mm});
            skArc(sketch, "E79.3", {"start": v(-60, -40.3) * mm, "mid": v(-58.99, -44.68) * mm, "end": v(-56.15, -48.18) * mm});
            skArc(sketch, "E79.4", {"start": v(-56.15, -48.18) * mm, "mid": v(0, -67.5) * mm, "end": v(56.15, -48.18) * mm});
            skArc(sketch, "E79.5", {"start": v(56.15, -48.18) * mm, "mid": v(58.99, -44.68) * mm, "end": v(60, -40.3) * mm});
            skLineSegment(sketch, "E79.6", {"start": v(60, 40.3) * mm, "end": v(60, -40.3) * mm});
            skArc(sketch, "E79.7", {"start": v(60, 40.3) * mm, "mid": v(58.99, 44.68) * mm, "end": v(56.15, 48.18) * mm});
            skCircle(sketch, "E79.8", {"center": v(-60, 67.5) * mm, "radius": 4 * mm});
            skCircle(sketch, "E79.9", {"center": v(-60, -67.5) * mm, "radius": 4 * mm});
            skCircle(sketch, "E79.10", {"center": v(60, -67.5) * mm, "radius": 4 * mm});
            skCircle(sketch, "E79.11", {"center": v(60, 67.5) * mm, "radius": 4 * mm});
            skArc(sketch, "E79.12", {"start": v(80, 80) * mm, "mid": v(77.07, 87.07) * mm, "end": v(70, 90) * mm});
            skLineSegment(sketch, "E79.13", {"start": v(-70, 90) * mm, "end": v(70, 90) * mm});
            skArc(sketch, "E79.14", {"start": v(-70, 90) * mm, "mid": v(-77.07, 87.07) * mm, "end": v(-80, 80) * mm});
            skLineSegment(sketch, "E79.15", {"start": v(-80, -80) * mm, "end": v(-80, 80) * mm});
            skArc(sketch, "E79.16", {"start": v(-80, -80) * mm, "mid": v(-77.07, -87.07) * mm, "end": v(-70, -90) * mm});
            skLineSegment(sketch, "E79.17", {"start": v(-70, -90) * mm, "end": v(70, -90) * mm});
            skArc(sketch, "E79.18", {"start": v(70, -90) * mm, "mid": v(77.07, -87.07) * mm, "end": v(80, -80) * mm});
            skLineSegment(sketch, "E79.19", {"start": v(80, -80) * mm, "end": v(80, 80) * mm});
            skLineSegment(sketch, "E80", {"start": v(-32.9, 90) * mm, "end": v(-14.9, 108) * mm});
            skLineSegment(sketch, "E81", {"start": v(15.1, 107.57) * mm, "end": v(15.1, 119.9) * mm});
            skLineSegment(sketch, "E82", {"start": v(-14.9, 108) * mm, "end": v(-14.9, 120) * mm});
            skArc(sketch, "E83", {"start": v(15.1, 119.9) * mm, "mid": v(0.15, 135) * mm, "end": v(-14.9, 120) * mm});
            skCircle(sketch, "E84", {"center": v(0.1, 120) * mm, "radius": 6 * mm});
            skLineSegment(sketch, "E85", {"start": v(0.1, 120) * mm, "end": v(0.1, 90) * mm, "construction": true});
            skLineSegment(sketch, "E86", {"start": v(15.1, 107.57) * mm, "end": v(32.66, 90) * mm});
            skLineSegment(sketch, "E87", {"start": v(-80, 0) * mm, "end": v(80, 0) * mm});
            skArc(sketch, "E88.MirrorCS", {"start": v(15.1, -119.9) * mm, "mid": v(0.15, -135) * mm, "end": v(-14.9, -120) * mm});
            skLineSegment(sketch, "E89.MirrorCS", {"start": v(-14.9, -108) * mm, "end": v(-14.9, -120) * mm});
            skLineSegment(sketch, "E90.MirrorCS", {"start": v(-32.9, -90) * mm, "end": v(-14.9, -108) * mm});
            skLineSegment(sketch, "E91.MirrorCS", {"start": v(0.1, -120) * mm, "end": v(0.1, -90) * mm, "construction": true});
            skCircle(sketch, "E92.MirrorC", {"center": v(0.1, -120) * mm, "radius": 6 * mm});
            skLineSegment(sketch, "E93.MirrorCS", {"start": v(15.1, -107.57) * mm, "end": v(15.1, -119.9) * mm});
            skLineSegment(sketch, "E94.MirrorCS", {"start": v(15.1, -107.57) * mm, "end": v(32.66, -90) * mm});
            skSolve(sketch);
        }
        {
            var Q0;
            Q0 = qSketchRegion(id + "F16", true);
            extrude(context, id + "F17", {"entities" : qUnion([Q0]), "endBound" : BoundingType.SYMMETRIC, "depth" : 6.5 * mm});
        }
    });
